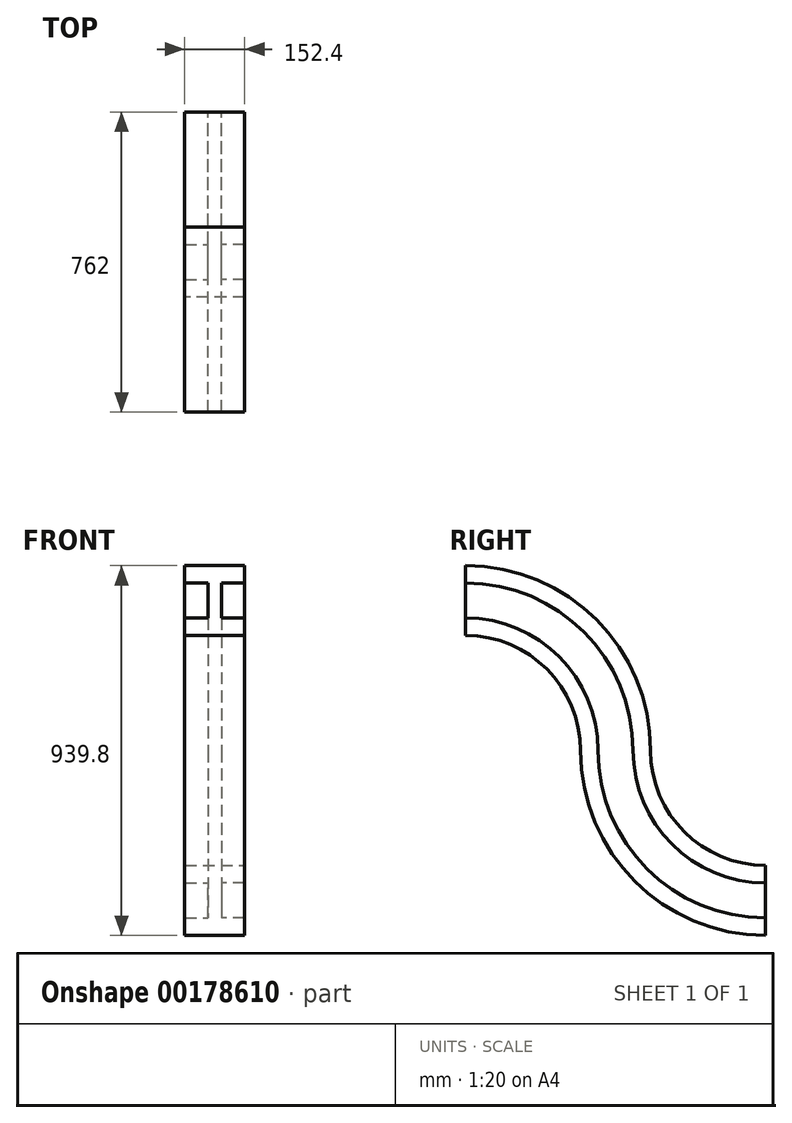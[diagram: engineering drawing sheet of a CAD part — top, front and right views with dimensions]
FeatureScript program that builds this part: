
annotation { "Feature Type Name" : "Feature", "Feature Type Description" : "" }
export const myFeature = defineFeature(function(context is Context, id is Id, definition is map)
    precondition{}
    {
        {
            var Q0;
            Q0=qCreatedBy(makeId("Front.planeOp"),FACE);
            var sketch = newSketch(context, id + "F0", { "sketchPlane" : qUnion([Q0])});
            skLineSegment(sketch, "E0", {"start": v(0, 88.9) * mm, "end": v(76.2, 88.9) * mm});
            skLineSegment(sketch, "E1", {"start": v(76.2, 88.9) * mm, "end": v(76.2, 44.45) * mm});
            skLineSegment(sketch, "E2", {"start": v(76.2, 44.45) * mm, "end": v(17.37, 44.45) * mm});
            skLineSegment(sketch, "E3", {"start": v(0, 88.9) * mm, "end": v(0, -88.9) * mm, "construction": true});
            skLineSegment(sketch, "E4", {"start": v(-17.37, 0) * mm, "end": v(17.37, 0) * mm, "construction": true});
            skLineSegment(sketch, "E5", {"start": v(17.37, 0) * mm, "end": v(17.37, 44.45) * mm});
            skLineSegment(sketch, "E6.MirrorCS", {"start": v(0, 88.9) * mm, "end": v(-76.2, 88.9) * mm});
            skLineSegment(sketch, "E7.MirrorCS", {"start": v(-76.2, 88.9) * mm, "end": v(-76.2, 44.45) * mm});
            skLineSegment(sketch, "E8.MirrorCS", {"start": v(-17.37, 0) * mm, "end": v(-17.37, 44.45) * mm});
            skLineSegment(sketch, "E9.MirrorCS", {"start": v(-76.2, 44.45) * mm, "end": v(-17.37, 44.45) * mm});
            skLineSegment(sketch, "E10.MirrorCS", {"start": v(0, -88.9) * mm, "end": v(-76.2, -88.9) * mm});
            skLineSegment(sketch, "E11.MirrorCS", {"start": v(-76.2, -88.9) * mm, "end": v(-76.2, -44.45) * mm});
            skLineSegment(sketch, "E12.MirrorCS", {"start": v(-76.2, -44.45) * mm, "end": v(-17.37, -44.45) * mm});
            skLineSegment(sketch, "E13.MirrorCS", {"start": v(-17.37, 0) * mm, "end": v(-17.37, -44.45) * mm});
            skLineSegment(sketch, "E14.MirrorCS", {"start": v(76.2, -44.45) * mm, "end": v(17.37, -44.45) * mm});
            skLineSegment(sketch, "E15.MirrorCS", {"start": v(0, -88.9) * mm, "end": v(76.2, -88.9) * mm});
            skLineSegment(sketch, "E16.MirrorCS", {"start": v(17.37, 0) * mm, "end": v(17.37, -44.45) * mm});
            skLineSegment(sketch, "E17.MirrorCS", {"start": v(76.2, -88.9) * mm, "end": v(76.2, -44.45) * mm});
            skSolve(sketch);
        }
        {
            var Q0;
            Q0=qCreatedBy(makeId("Right.planeOp"),FACE);
            var sketch = newSketch(context, id + "F1", { "sketchPlane" : qUnion([Q0])});
            skArc(sketch, "E18", {"start": v(0, 0) * mm, "mid": v(269.4, -111.6) * mm, "end": v(381, -381) * mm});
            skArc(sketch, "E19", {"start": v(381, -381) * mm, "mid": v(492.6, -650.4) * mm, "end": v(762, -762) * mm});
            skSolve(sketch);
        }
        {
            var Q0;
            Q0=makeQuery(id+"F0.imprint","IMPRINT",FACE,{"disambiguationData":[TD([[makeQuery(id+"F0.imprint","IMPRINT",EDGE,{"derivedFrom":sQuery(id+"F0.wireOp",EDGE,"E0")}),-1.0]])]});
            var Q1;
            Q1 = qConstructionFilter(qBodyType(qCreatedBy(id + "F1" ,EDGE), BodyType.WIRE), ConstructionObject.NO);
            sweep(context, id + "F2", {"profiles" : qUnion([Q0]), "path" : qUnion([Q1])});
        }
        {
            var Q0;
            Q0=makeQuery(id+"F0.imprint","IMPRINT",FACE,{"disambiguationData":[TD([[makeQuery(id+"F0.imprint","IMPRINT",EDGE,{"derivedFrom":sQuery(id+"F0.wireOp",EDGE,"E0")}),-1.0]])]});
            var Q1;
            Q1=sQuery(id+"F1.wireOp",EDGE,"E18");
            var Q2;
            Q2=sQuery(id+"F1.wireOp",EDGE,"E19");
            sweep(context, id + "F3", {"profiles" : qUnion([Q0]), "path" : qUnion([Q1, Q2])});
        }
    });
